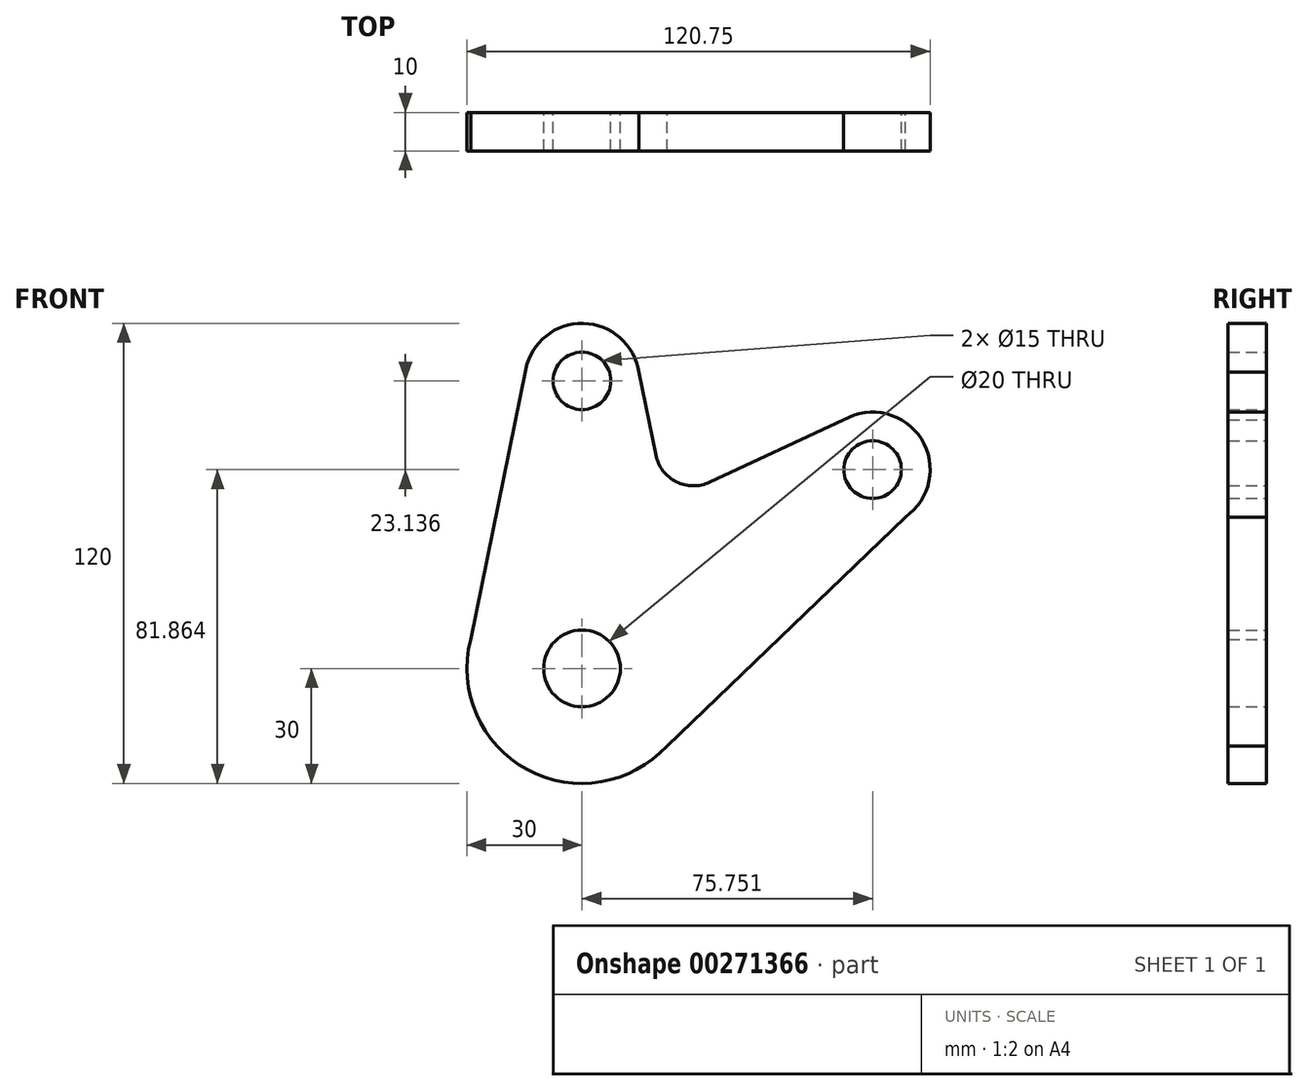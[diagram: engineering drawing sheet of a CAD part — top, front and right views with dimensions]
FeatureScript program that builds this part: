
annotation { "Feature Type Name" : "Feature", "Feature Type Description" : "" }
export const myFeature = defineFeature(function(context is Context, id is Id, definition is map)
    precondition{}
    {
        {
            var Q0;
            Q0=qCreatedBy(makeId("Front.planeOp"),FACE);
            var sketch = newSketch(context, id + "F0", { "sketchPlane" : qUnion([Q0])});
            skCircle(sketch, "E0", {"center": v(0, 0) * mm, "radius": 10 * mm});
            skCircle(sketch, "E1", {"center": v(0, 75) * mm, "radius": 7.5 * mm});
            skArc(sketch, "E2", {"start": v(14.82, 77.29) * mm, "mid": v(0.36, 90) * mm, "end": v(-14.7, 78) * mm});
            skCircle(sketch, "E3", {"center": v(75.75, 51.86) * mm, "radius": 7.5 * mm});
            skArc(sketch, "E4", {"start": v(84.24, 39.5) * mm, "mid": v(88.43, 59.88) * mm, "end": v(68.22, 64.84) * mm});
            skLineSegment(sketch, "E5", {"start": v(68.22, 64.84) * mm, "end": v(33.27, 48.57) * mm});
            skLineSegment(sketch, "E6", {"start": v(14.82, 77.29) * mm, "end": v(19.25, 55.63) * mm});
            skArc(sketch, "E7.filletArc", {"start": v(19.25, 55.63) * mm, "mid": v(24.55, 48.7) * mm, "end": v(33.27, 48.57) * mm});
            skArc(sketch, "E8", {"start": v(-29.05, 7.5) * mm, "mid": v(-14.29, -26.38) * mm, "end": v(22.15, -20.23) * mm});
            skLineSegment(sketch, "E9", {"start": v(22.15, -20.23) * mm, "end": v(87.78, 42.9) * mm});
            skLineSegment(sketch, "E10", {"start": v(-29.67, 4.45) * mm, "end": v(-14.7, 78) * mm});
            skSolve(sketch);
        }
        {
            var Q0;
            Q0 = qSketchRegion(id + "F0", true);
            extrude(context, id + "F1", {"entities" : qUnion([Q0]), "depth" : 10 * mm});
        }
    });
